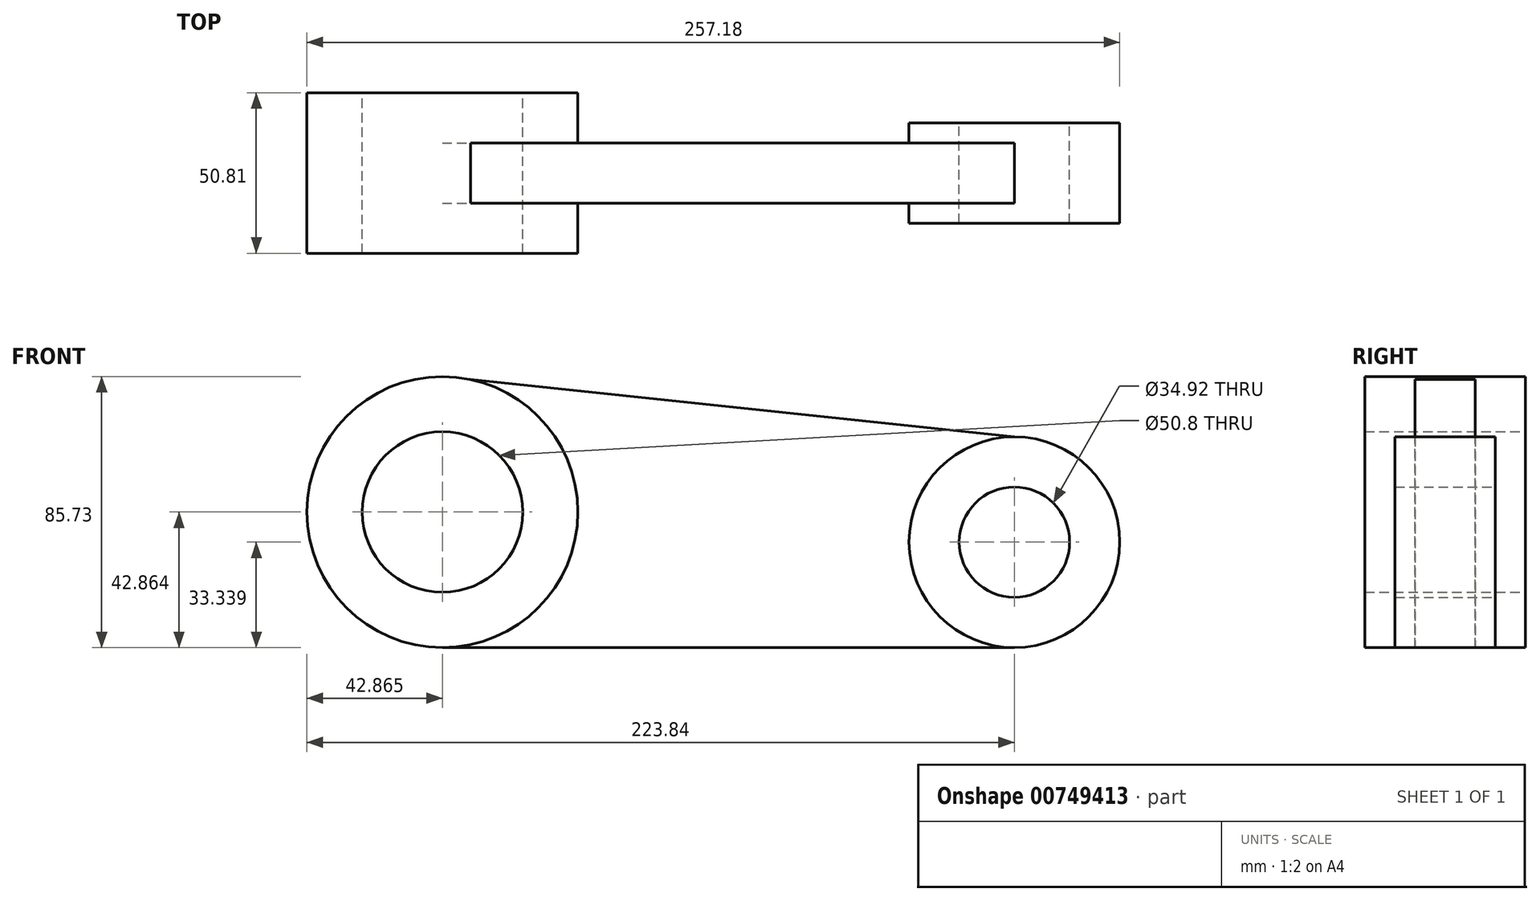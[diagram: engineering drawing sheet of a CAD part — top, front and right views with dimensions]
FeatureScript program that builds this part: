
annotation { "Feature Type Name" : "Feature", "Feature Type Description" : "" }
export const myFeature = defineFeature(function(context is Context, id is Id, definition is map)
    precondition{}
    {
        {
            var Q0;
            Q0=qCreatedBy(makeId("Front.planeOp"),FACE);
            var sketch = newSketch(context, id + "F0", { "sketchPlane" : qUnion([Q0])});
            skCircle(sketch, "E0", {"center": v(-57.77, 11.78) * mm, "radius": 25.4 * mm});
            skCircle(sketch, "E1", {"center": v(-57.77, 11.78) * mm, "radius": 42.86 * mm});
            skLineSegment(sketch, "E2", {"start": v(-57.77, -31.08) * mm, "end": v(123.2, -31.08) * mm});
            skCircle(sketch, "E3", {"center": v(123.2, 2.26) * mm, "radius": 33.34 * mm});
            skCircle(sketch, "E4", {"center": v(123.2, 2.26) * mm, "radius": 17.46 * mm});
            skLineSegment(sketch, "E5", {"start": v(123.2, 35.6) * mm, "end": v(-57.77, 54.65) * mm});
            skSolve(sketch);
        }
        {
            var Q0;
            Q0 = qSketchRegion(id + "F0", true);
            extrude(context, id + "F1", {"entities" : qUnion([Q0]), "depth" : 19.05 * mm, "offsetDistance" : 25.4 * mm});
        }
        {
            var Q0;
            Q0=makeQuery(id+"F1.opExtrude","CAP_FACE",FACE,{"disambiguationData":[OSD([sQuery(id+"F0.wireOp",EDGE,"E0"),sQuery(id+"F0.wireOp",EDGE,"E1"),sQuery(id+"F0.wireOp",EDGE,"E2"),sQuery(id+"F0.wireOp",EDGE,"E3"),sQuery(id+"F0.wireOp",EDGE,"E4"),sQuery(id+"F0.wireOp",EDGE,"E5")])],"isStart":false});
            var sketch = newSketch(context, id + "F2", { "sketchPlane" : qUnion([Q0])});
            skCircle(sketch, "E6", {"center": v(-57.77, 11.78) * mm, "radius": 42.86 * mm});
            skSolve(sketch);
        }
        {
            var Q0;
            Q0 = qSketchRegion(id + "F2", true);
            extrude(context, id + "F3", {"entities" : qUnion([Q0]), "operationType" : NewBodyOperationType.ADD, "depth" : 15.88 * mm, "offsetDistance" : 25.4 * mm});
        }
        {
            var Q0;
            Q0=makeQuery(id+"F3.opExtrude","CAP_FACE",FACE,{"disambiguationData":[OSD([sQuery(id+"F2.wireOp",EDGE,"E6")])],"isStart":false});
            var sketch = newSketch(context, id + "F4", { "sketchPlane" : qUnion([Q0])});
            skCircle(sketch, "E7", {"center": v(-57.77, 11.78) * mm, "radius": 25.4 * mm});
            skSolve(sketch);
        }
        {
            var Q0;
            Q0 = qSketchRegion(id + "F4", true);
            extrude(context, id + "F5", {"entities" : qUnion([Q0]), "operationType" : NewBodyOperationType.REMOVE, "oppositeDirection" : true, "depth" : 84.84 * mm, "offsetDistance" : 25.4 * mm});
        }
        {
            var Q0;
            Q0=makeQuery(id+"F1.opExtrude","CAP_FACE",FACE,{"disambiguationData":[OSD([sQuery(id+"F0.wireOp",EDGE,"E0"),sQuery(id+"F0.wireOp",EDGE,"E1"),sQuery(id+"F0.wireOp",EDGE,"E2"),sQuery(id+"F0.wireOp",EDGE,"E3"),sQuery(id+"F0.wireOp",EDGE,"E4"),sQuery(id+"F0.wireOp",EDGE,"E5")])],"isStart":true});
            var sketch = newSketch(context, id + "F6", { "sketchPlane" : qUnion([Q0])});
            skCircle(sketch, "E8", {"center": v(57.77, 11.78) * mm, "radius": 25.4 * mm});
            skCircle(sketch, "E9", {"center": v(57.77, 11.78) * mm, "radius": 42.86 * mm});
            skSolve(sketch);
        }
        {
            var Q0;
            Q0 = qSketchRegion(id + "F6", true);
            extrude(context, id + "F7", {"entities" : qUnion([Q0]), "operationType" : NewBodyOperationType.ADD, "depth" : 15.88 * mm, "offsetDistance" : 25.4 * mm});
        }
        {
            var Q0;
            Q0=makeQuery(id+"F1.opExtrude","CAP_FACE",FACE,{"disambiguationData":[OSD([sQuery(id+"F0.wireOp",EDGE,"E0"),sQuery(id+"F0.wireOp",EDGE,"E1"),sQuery(id+"F0.wireOp",EDGE,"E2"),sQuery(id+"F0.wireOp",EDGE,"E3"),sQuery(id+"F0.wireOp",EDGE,"E4"),sQuery(id+"F0.wireOp",EDGE,"E5")])],"isStart":false});
            var sketch = newSketch(context, id + "F8", { "sketchPlane" : qUnion([Q0])});
            skCircle(sketch, "E10", {"center": v(123.2, 2.26) * mm, "radius": 17.46 * mm});
            skCircle(sketch, "E11", {"center": v(123.2, 2.26) * mm, "radius": 33.34 * mm});
            skSolve(sketch);
        }
        {
            var Q0;
            Q0 = qSketchRegion(id + "F8", true);
            extrude(context, id + "F9", {"entities" : qUnion([Q0]), "operationType" : NewBodyOperationType.ADD, "depth" : 6.35 * mm, "offsetDistance" : 25.4 * mm});
        }
        {
            var Q0;
            Q0=makeQuery(id+"F1.opExtrude","CAP_FACE",FACE,{"disambiguationData":[OSD([sQuery(id+"F0.wireOp",EDGE,"E0"),sQuery(id+"F0.wireOp",EDGE,"E1"),sQuery(id+"F0.wireOp",EDGE,"E2"),sQuery(id+"F0.wireOp",EDGE,"E3"),sQuery(id+"F0.wireOp",EDGE,"E4"),sQuery(id+"F0.wireOp",EDGE,"E5")])],"isStart":true});
            var sketch = newSketch(context, id + "F10", { "sketchPlane" : qUnion([Q0])});
            skCircle(sketch, "E12", {"center": v(-123.2, 2.26) * mm, "radius": 17.46 * mm});
            skCircle(sketch, "E13", {"center": v(-123.2, 2.26) * mm, "radius": 33.34 * mm});
            skSolve(sketch);
        }
        {
            var Q0;
            Q0 = qSketchRegion(id + "F10", true);
            extrude(context, id + "F11", {"entities" : qUnion([Q0]), "operationType" : NewBodyOperationType.ADD, "depth" : 6.35 * mm, "offsetDistance" : 25.4 * mm});
        }
    });
